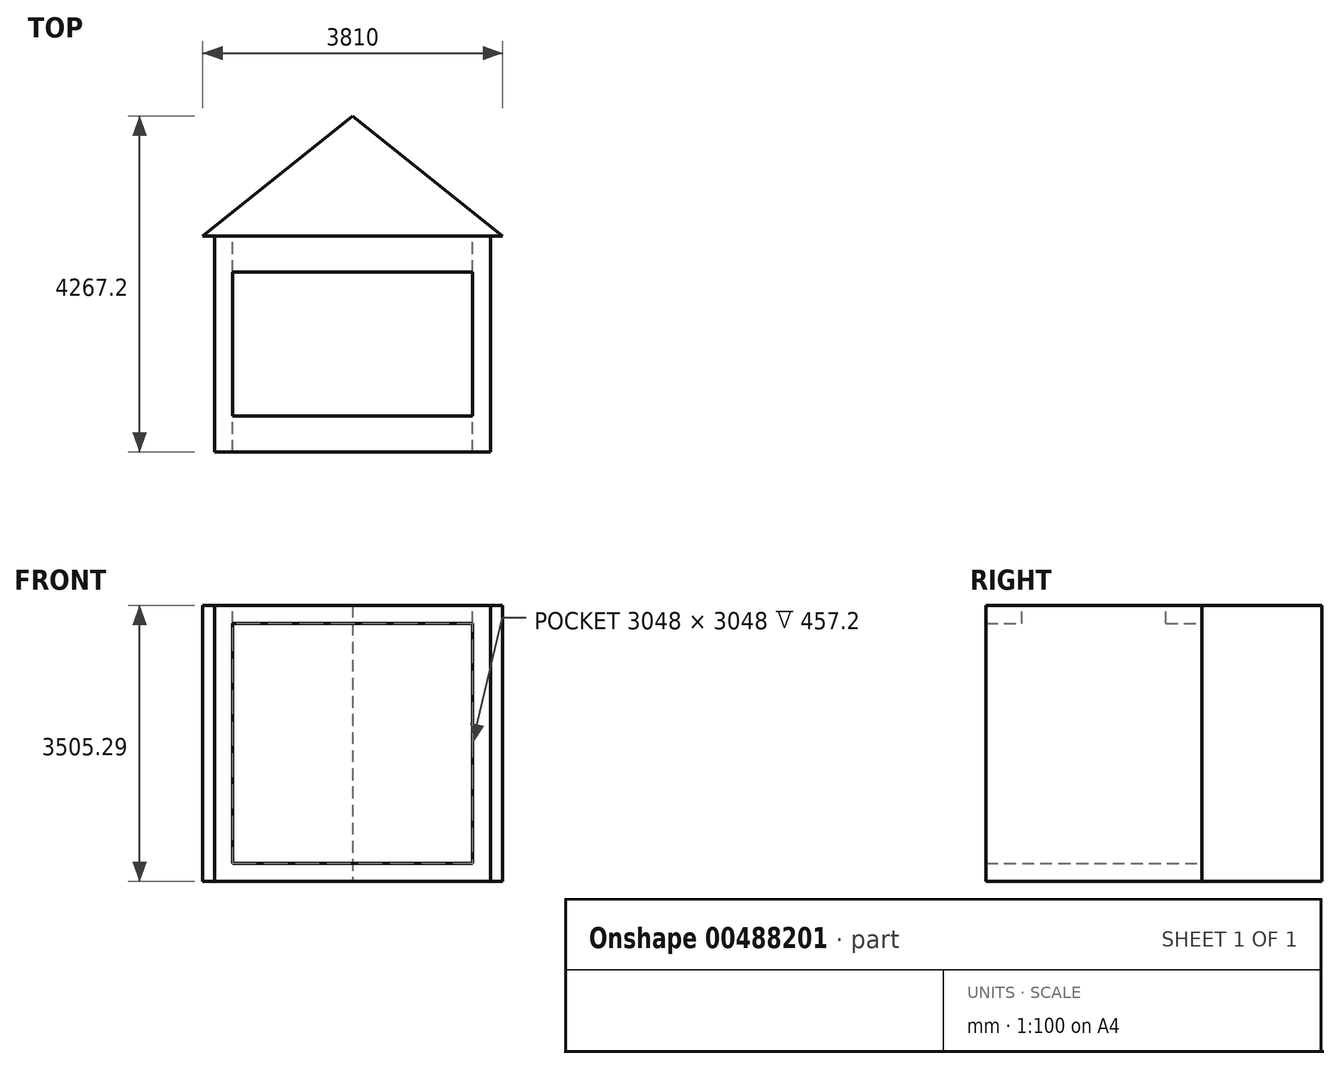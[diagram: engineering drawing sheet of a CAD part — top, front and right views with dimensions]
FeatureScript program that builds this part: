
annotation { "Feature Type Name" : "Feature", "Feature Type Description" : "" }
export const myFeature = defineFeature(function(context is Context, id is Id, definition is map)
    precondition{}
    {
        {
            var Q0;
            Q0=qCreatedBy(makeId("Front.planeOp"),FACE);
            var sketch = newSketch(context, id + "F0", { "sketchPlane" : qUnion([Q0])});
            skLineSegment(sketch, "E0.bottom", {"start": v(-1752.59, 1752.51) * mm, "end": v(1752.61, 1752.51) * mm});
            skLineSegment(sketch, "E0.top", {"start": v(-1752.59, -1752.69) * mm, "end": v(1752.61, -1752.69) * mm});
            skLineSegment(sketch, "E0.left", {"start": v(-1752.59, 1752.51) * mm, "end": v(-1752.59, -1752.69) * mm});
            skLineSegment(sketch, "E0.right", {"start": v(1752.61, 1752.51) * mm, "end": v(1752.61, -1752.69) * mm});
            skPoint(sketch, "E0.middle", {"position": v(0.01, -0.09) * mm});
            skLineSegment(sketch, "E1.bottom", {"start": v(1524.01, -1524.09) * mm, "end": v(-1523.99, -1524.09) * mm});
            skLineSegment(sketch, "E1.top", {"start": v(1524.01, 1523.91) * mm, "end": v(-1523.99, 1523.91) * mm});
            skLineSegment(sketch, "E1.left", {"start": v(1524.01, -1524.09) * mm, "end": v(1524.01, 1523.91) * mm});
            skLineSegment(sketch, "E1.right", {"start": v(-1523.99, -1524.09) * mm, "end": v(-1523.99, 1523.91) * mm});
            skSolve(sketch);
        }
        {
            var Q0;
            Q0=makeQuery(id+"F0.imprint","IMPRINT",FACE,{"disambiguationData":[TD([[makeQuery(id+"F0.imprint","IMPRINT",EDGE,{"derivedFrom":sQuery(id+"F0.wireOp",EDGE,"E0.bottom")}),-1.0]])]});
            extrude(context, id + "F1", {"entities" : qUnion([Q0]), "depth" : 2743.2 * mm});
        }
        {
            var Q0;
            Q0=qCreatedBy(makeId("Top.planeOp"),FACE);
            var sketch = newSketch(context, id + "F2", { "sketchPlane" : qUnion([Q0])});
            skLineSegment(sketch, "E2", {"start": v(-1904.99, 0) * mm, "end": v(0, 1524) * mm});
            skLineSegment(sketch, "E3", {"start": v(0, 1524) * mm, "end": v(1905.01, 0) * mm});
            skLineSegment(sketch, "E4", {"start": v(1905.01, 0) * mm, "end": v(-1904.99, 0) * mm});
            skSolve(sketch);
        }
        {
            var Q0;
            Q0=makeQuery(id+"F2.imprint","IMPRINT",FACE,{"disambiguationData":[TD([[makeQuery(id+"F2.imprint","IMPRINT",EDGE,{"derivedFrom":sQuery(id+"F2.wireOp",EDGE,"E2")}),-1.0]])]});
            extrude(context, id + "F3", {"entities" : qUnion([Q0]), "operationType" : NewBodyOperationType.ADD, "endBound" : BoundingType.SYMMETRIC, "depth" : 3505.2 * mm});
        }
        {
            var Q0;
            Q0=makeQuery(id+"F1.opExtrude","SWEPT_FACE",FACE,{"disambiguationData":[OSD([sQuery(id+"F0.wireOp",EDGE,"E0.bottom")])]});
            var sketch = newSketch(context, id + "F4", { "sketchPlane" : qUnion([Q0])});
            skLineSegment(sketch, "E5.bottom", {"start": v(-1523.99, -457.2) * mm, "end": v(1524.01, -457.2) * mm});
            skLineSegment(sketch, "E5.top", {"start": v(-1523.99, -2286) * mm, "end": v(1524.01, -2286) * mm});
            skLineSegment(sketch, "E5.left", {"start": v(-1523.99, -457.2) * mm, "end": v(-1523.99, -2286) * mm});
            skLineSegment(sketch, "E5.right", {"start": v(1524.01, -457.2) * mm, "end": v(1524.01, -2286) * mm});
            skSolve(sketch);
        }
        {
            var Q0;
            Q0=makeQuery(id+"F4.imprint","IMPRINT",FACE,{"disambiguationData":[TD([[makeQuery(id+"F4.imprint","IMPRINT",EDGE,{"derivedFrom":sQuery(id+"F4.wireOp",EDGE,"E5.bottom")}),-1.0]])]});
            extrude(context, id + "F5", {"entities" : qUnion([Q0]), "operationType" : NewBodyOperationType.REMOVE, "oppositeDirection" : true, "depth" : 304.8 * mm});
        }
    });
